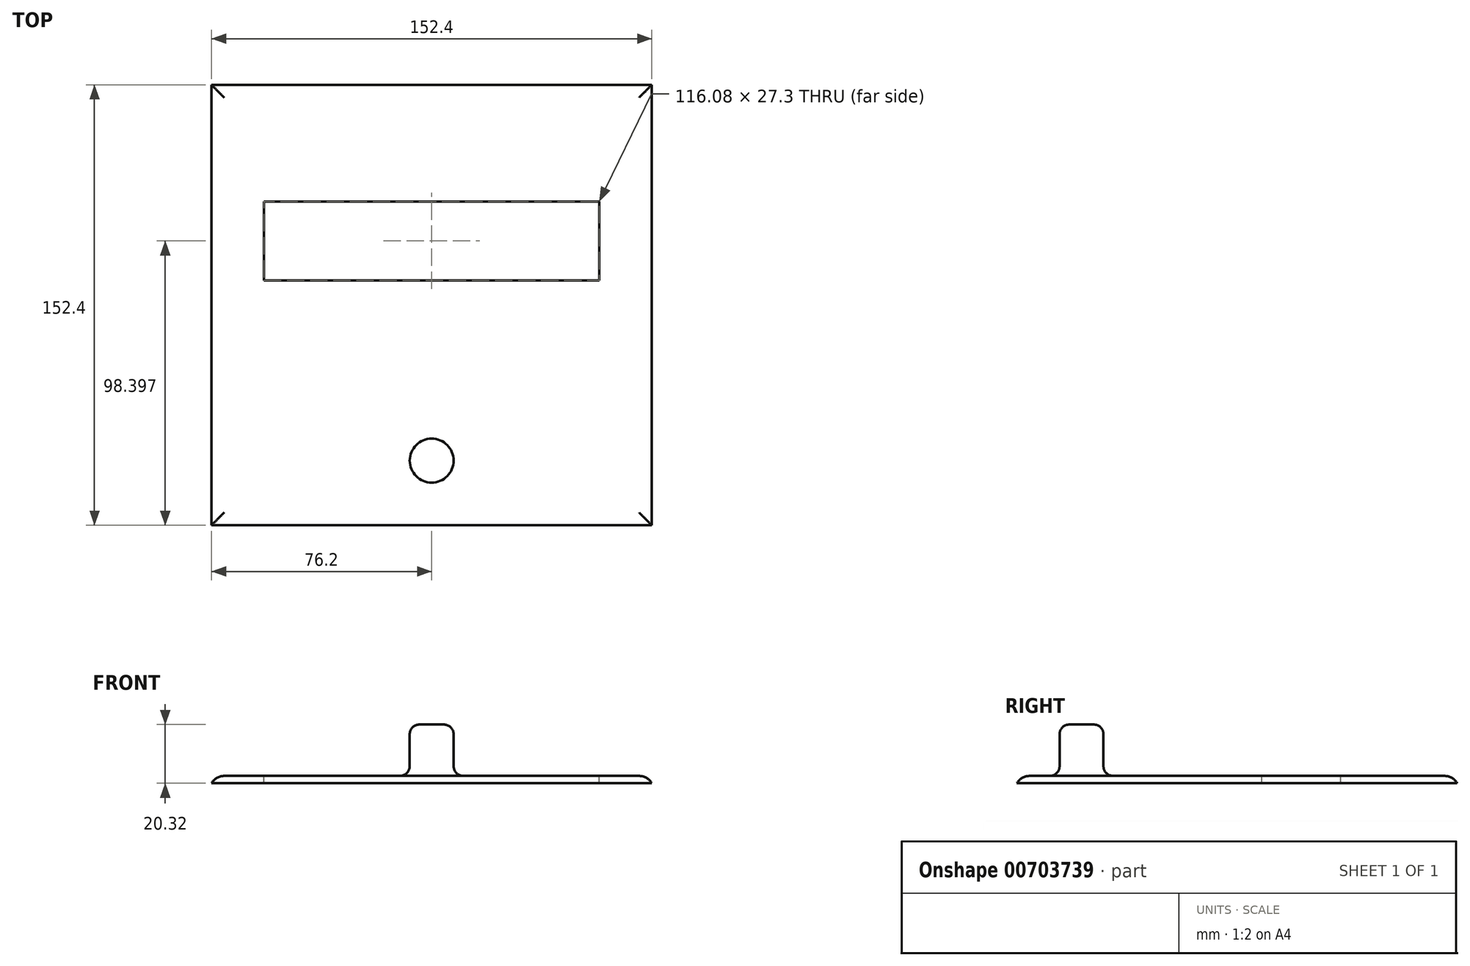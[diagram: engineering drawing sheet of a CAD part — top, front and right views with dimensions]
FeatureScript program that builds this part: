
annotation { "Feature Type Name" : "Feature", "Feature Type Description" : "" }
export const myFeature = defineFeature(function(context is Context, id is Id, definition is map)
    precondition{}
    {
        {
            var Q0;
            Q0=qCreatedBy(makeId("Front.planeOp"),FACE);
            var sketch = newSketch(context, id + "F0", { "sketchPlane" : qUnion([Q0])});
            skLineSegment(sketch, "E0.bottom", {"start": v(-76.2, -1.27) * mm, "end": v(76.2, -1.27) * mm});
            skLineSegment(sketch, "E0.top", {"start": v(-76.2, 1.27) * mm, "end": v(76.2, 1.27) * mm});
            skLineSegment(sketch, "E0.left", {"start": v(-76.2, -1.27) * mm, "end": v(-76.2, 1.27) * mm});
            skLineSegment(sketch, "E0.right", {"start": v(76.2, -1.27) * mm, "end": v(76.2, 1.27) * mm});
            skPoint(sketch, "E0.middle", {"position": v(0, 0) * mm});
            skSolve(sketch);
        }
        {
            var Q0;
            Q0 = qSketchRegion(id + "F0", true);
            var Q1;
            Q1=makeQuery(id+"F0.imprint","IMPRINT",FACE,{"disambiguationData":[TD([[makeQuery(id+"F0.imprint","IMPRINT",EDGE,{"derivedFrom":sQuery(id+"F0.wireOp",EDGE,"E0.bottom")}),1.0]])]});
            extrude(context, id + "F1", {"entities" : qUnion([Q0, Q1]), "oppositeDirection" : true, "depth" : 76.2 * mm, "offsetDistance" : 25.4 * mm, "hasSecondDirection" : true, "secondDirectionOppositeDirection" : false, "secondDirectionDepth" : 76.2 * mm});
        }
        {
            var Q0;
            Q0=makeQuery(id+"F1.opExtrude","SWEPT_FACE",FACE,{"disambiguationData":[OSD([sQuery(id+"F0.wireOp",EDGE,"E0.top")])]});
            var sketch = newSketch(context, id + "F2", { "sketchPlane" : qUnion([Q0])});
            skLineSegment(sketch, "E1.bottom", {"start": v(-58.04, 35.85) * mm, "end": v(58.04, 35.85) * mm});
            skLineSegment(sketch, "E1.top", {"start": v(-58.04, 8.55) * mm, "end": v(58.04, 8.55) * mm});
            skLineSegment(sketch, "E1.left", {"start": v(-58.04, 35.85) * mm, "end": v(-58.04, 8.55) * mm});
            skLineSegment(sketch, "E1.right", {"start": v(58.04, 35.85) * mm, "end": v(58.04, 8.55) * mm});
            skPoint(sketch, "E1.middle", {"position": v(0, 22.2) * mm});
            skSolve(sketch);
        }
        {
            var Q0;
            Q0=makeQuery(id+"F2.imprint","IMPRINT",FACE,{"disambiguationData":[TD([[makeQuery(id+"F2.imprint","IMPRINT",EDGE,{"derivedFrom":sQuery(id+"F2.wireOp",EDGE,"E1.bottom")}),-1.0]])]});
            var Q1;
            Q1 = qSketchRegion(id + "F2", true);
            extrude(context, id + "F3", {"entities" : qUnion([Q0, Q1]), "operationType" : NewBodyOperationType.REMOVE, "oppositeDirection" : true, "depth" : 25.4 * mm, "offsetDistance" : 25.4 * mm});
        }
        {
            var Q0;
            Q0=makeQuery(id+"F1.opExtrude","SWEPT_FACE",FACE,{"disambiguationData":[OSD([sQuery(id+"F0.wireOp",EDGE,"E0.top")])]});
            var sketch = newSketch(context, id + "F4", { "sketchPlane" : qUnion([Q0])});
            skCircle(sketch, "E2", {"center": v(0, -53.84) * mm, "radius": 7.6 * mm});
            skSolve(sketch);
        }
        {
            var Q0;
            Q0 = qSketchRegion(id + "F4", true);
            var Q1;
            Q1=makeQuery(id+"F4.imprint","IMPRINT",FACE,{"disambiguationData":[TD([[makeQuery(id+"F4.imprint","IMPRINT",EDGE,{"derivedFrom":sQuery(id+"F4.wireOp",EDGE,"E2")}),1.0]])]});
            extrude(context, id + "F5", {"entities" : qUnion([Q0, Q1]), "operationType" : NewBodyOperationType.ADD, "depth" : 17.78 * mm, "offsetDistance" : 25.4 * mm});
        }
        {
            var Q0;
            Q0=makeQuery(id+"F5.opExtrude","SWEPT_FACE",FACE,{"disambiguationData":[OSD([sQuery(id+"F4.wireOp",EDGE,"E2")])]});
            fillet(context, id + "F6", {"entities" : qUnion([Q0]), "radius" : 3.36 * mm, "tangentPropagation" : true, "allowEdgeOverflow" : false});
        }
        {
            var Q0;
            Q0=makeQuery(id+"F1.opExtrude","CAP_EDGE",EDGE,{"disambiguationData":[OSD([sQuery(id+"F0.wireOp",EDGE,"E0.top")])],"isStart":true});
            var Q1;
            Q1=makeQuery(id+"F1.opExtrude","SWEPT_EDGE",EDGE,{"disambiguationData":[OSD([sQuery(id+"F0.wireOp",EDGE,"E0.top"),sQuery(id+"F0.wireOp",EDGE,"E0.right")])]});
            var Q2;
            Q2=makeQuery(id+"F1.opExtrude","CAP_EDGE",EDGE,{"disambiguationData":[OSD([sQuery(id+"F0.wireOp",EDGE,"E0.top")])],"isStart":false});
            var Q3;
            Q3=makeQuery(id+"F1.opExtrude","SWEPT_EDGE",EDGE,{"disambiguationData":[OSD([sQuery(id+"F0.wireOp",EDGE,"E0.top"),sQuery(id+"F0.wireOp",EDGE,"E0.left")])]});
            fillet(context, id + "F7", {"entities" : qUnion([Q0, Q1, Q2, Q3]), "radius" : 5.08 * mm, "tangentPropagation" : true, "allowEdgeOverflow" : false});
        }
    });
